# Revit family: БП8П_RV17_LOD400 (05.11.23)
name_source: partatom
category: Электрооборудование
revit_build: Autodesk Revit 2017 (Build: 20170118_1100(x64)
units: mm (PartAtom-declared; Revit-internal decimal feet)

## family parameters
Всегда вертикально = Нет
Конфигурация панели = Два столбца, слева направо
На основе рабочей плоскости = Да
Общий = Нет
При загрузке вырезать с полостями = Нет
Размер круглого соединителя = Использовать диаметр
Тип детали = Щит
Точка расчета площади = Нет

## types (1)
- БК8П
    ADSK_URL страницы изделия = https://stilsoft.ru
    ADSK_Единица измерения = шт.
    ADSK_Завод-изготовитель = ООО «Основа Безопасности»
    ADSK_Количество = 1
    ADSK_Марка = СТВФ.426471.089-02ПС
СТВФ.426471.089-02ПС
СТВФ.426471.089-02
    ADSK_Масса = 3
    ADSK_Наименование = Коммутатор БК8П
    ADSK_Размер_Высота = 84 мм
    ADSK_Размер_Глубина = 152 мм
    ADSK_Размер_Ширина = 295 мм
    d_короба = 20 мм
    Время непрерывной работы, ч = круглосуточно
    Диапазон рабочих температур, °С = от – 40 до + 50
    Количество коммутируемых портов Auto MDI/MDIX с поддержкой РоЕ, шт. = 8
    Максимальная мощность РоЕ на один порт, Вт = 30
    Мощность = 210
    Напряжение = 220
    Отметка по умолчанию = 1219 мм
    Потребляемый ток, не более, А = 2 А
    Размер буфера пакетов, КБ = 512
    Размер таблицы MAC-адресов = 8К
    Стандарт РоЕ = IEEE 802.3 af/at
    Стандарт интерфейса связи = 10/ 100 / 1000 Base-T Ethernet
    Степень защиты от внешних воздействий в составе контроллера STS-504 = IP54
